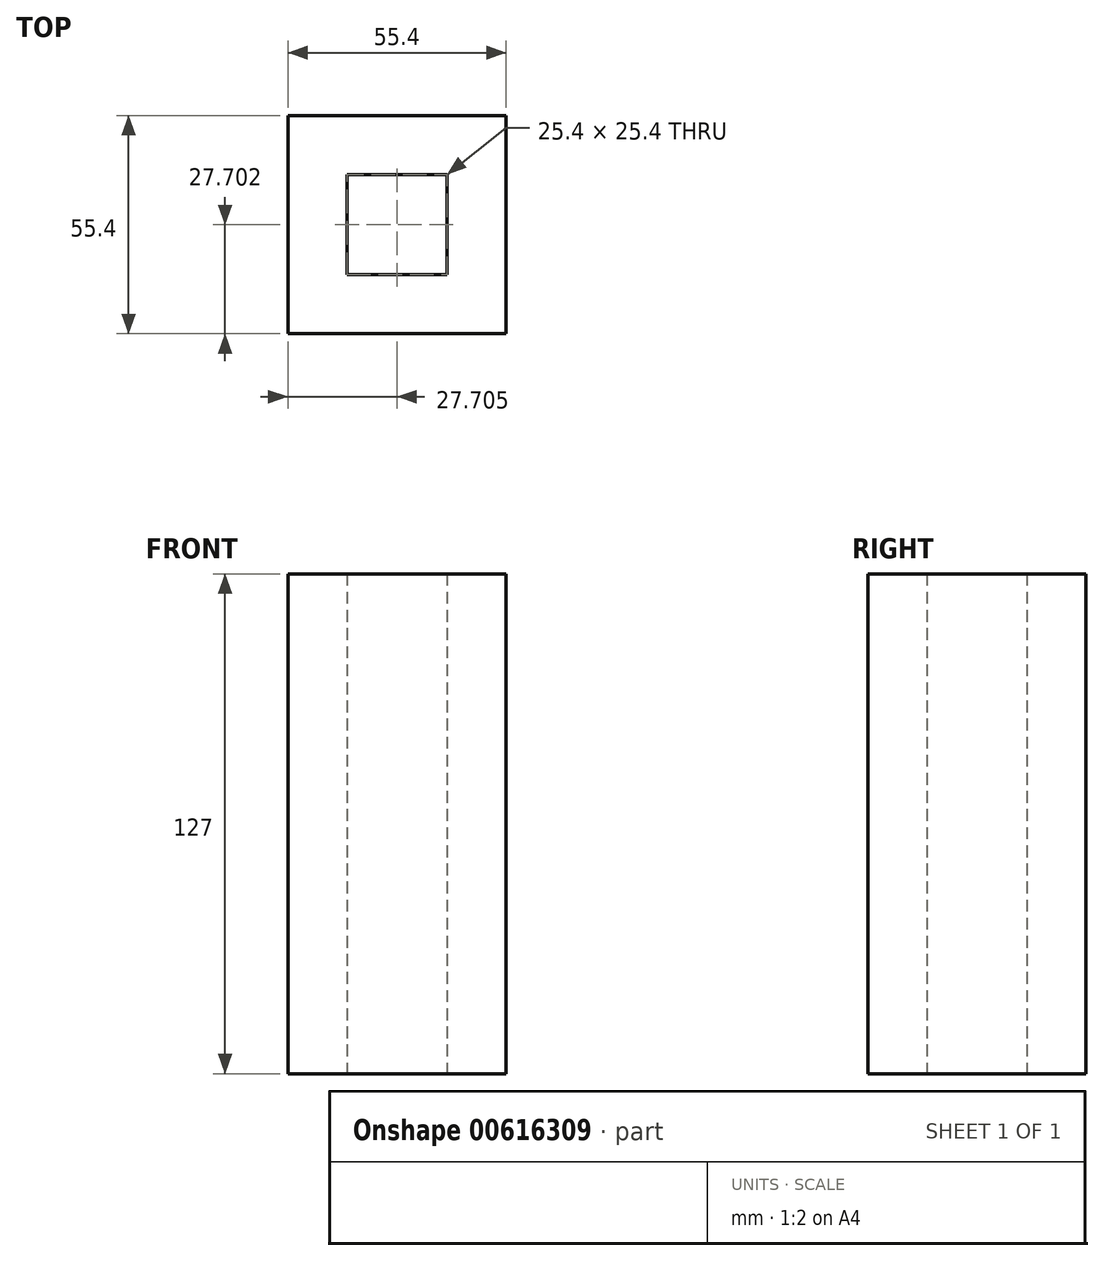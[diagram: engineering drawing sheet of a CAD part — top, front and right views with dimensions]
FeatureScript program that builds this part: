
annotation { "Feature Type Name" : "Feature", "Feature Type Description" : "" }
export const myFeature = defineFeature(function(context is Context, id is Id, definition is map)
    precondition{}
    {
        {
            var Q0;
            Q0=qCreatedBy(makeId("Top.planeOp"),FACE);
            var sketch = newSketch(context, id + "F0", { "sketchPlane" : qUnion([Q0])});
            skLineSegment(sketch, "E0.bottom", {"start": v(-54.3, 1.51) * mm, "end": v(-28.9, 1.51) * mm});
            skLineSegment(sketch, "E0.top", {"start": v(-54.3, -23.89) * mm, "end": v(-28.9, -23.89) * mm});
            skLineSegment(sketch, "E0.left", {"start": v(-54.3, 1.51) * mm, "end": v(-54.3, -23.89) * mm});
            skLineSegment(sketch, "E0.right", {"start": v(-28.9, 1.51) * mm, "end": v(-28.9, -23.89) * mm});
            skLineSegment(sketch, "E1.0", {"start": v(-69.3, 16.51) * mm, "end": v(-69.3, -38.89) * mm});
            skLineSegment(sketch, "E1.1", {"start": v(-69.3, 16.51) * mm, "end": v(-13.9, 16.51) * mm});
            skLineSegment(sketch, "E1.2", {"start": v(-13.9, 16.51) * mm, "end": v(-13.9, -38.89) * mm});
            skLineSegment(sketch, "E1.3", {"start": v(-69.3, -38.89) * mm, "end": v(-13.9, -38.89) * mm});
            skLineSegment(sketch, "E2", {"start": v(-69.3, 16.51) * mm, "end": v(-54.3, 1.51) * mm});
            skLineSegment(sketch, "E3", {"start": v(-13.9, 16.51) * mm, "end": v(-28.9, 1.51) * mm});
            skLineSegment(sketch, "E4", {"start": v(-13.9, -38.89) * mm, "end": v(-28.9, -23.89) * mm});
            skLineSegment(sketch, "E5", {"start": v(-69.3, -38.89) * mm, "end": v(-54.3, -23.89) * mm});
            skSolve(sketch);
        }
        {
            var Q0;
            Q0 = qSketchRegion(id + "F0", true);
            extrude(context, id + "F1", {"entities" : qUnion([Q0]), "depth" : 25.4 * mm, "offsetDistance" : 25.4 * mm});
        }
        {
            var Q0;
            Q0 = qSketchRegion(id + "F0", true);
            extrude(context, id + "F2", {"entities" : qUnion([Q0]), "operationType" : NewBodyOperationType.ADD, "endBound" : BoundingType.SYMMETRIC, "depth" : 127 * mm, "offsetDistance" : 25.4 * mm});
        }
    });
